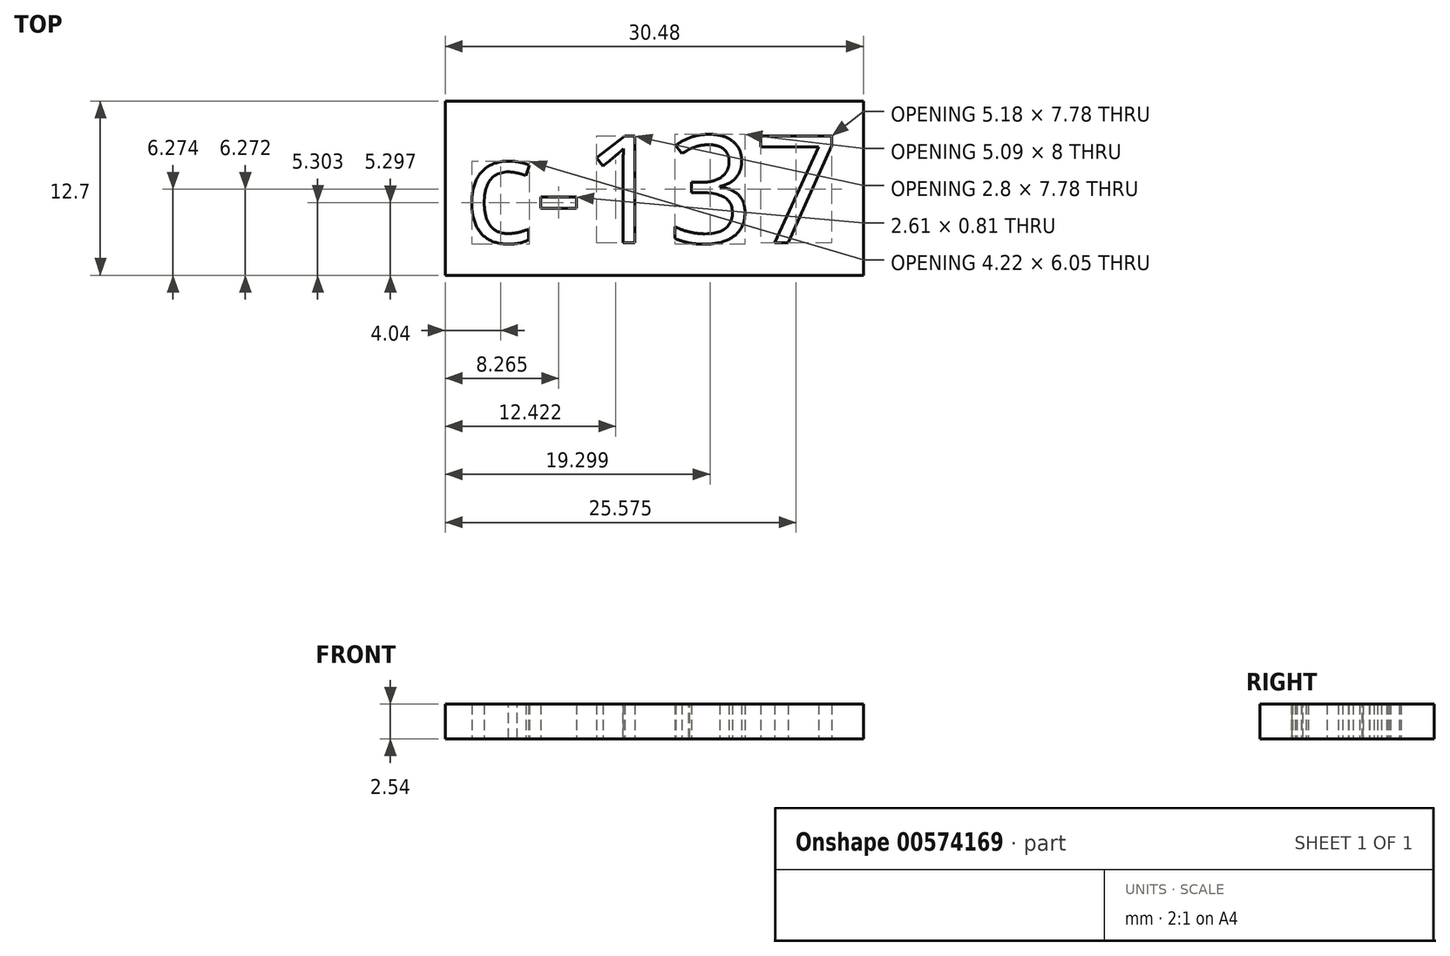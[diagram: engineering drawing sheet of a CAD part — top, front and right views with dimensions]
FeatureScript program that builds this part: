
annotation { "Feature Type Name" : "Feature", "Feature Type Description" : "" }
export const myFeature = defineFeature(function(context is Context, id is Id, definition is map)
    precondition{}
    {
        {
            var Q0;
            Q0=qCreatedBy(makeId("Top.planeOp"),FACE);
            var sketch = newSketch(context, id + "F0", { "sketchPlane" : qUnion([Q0])});
            skLineSegment(sketch, "E0.bottom", {"start": v(-16.62, 0) * mm, "end": v(13.86, 0) * mm});
            skLineSegment(sketch, "E0.top", {"start": v(-16.62, 12.7) * mm, "end": v(13.86, 12.7) * mm});
            skLineSegment(sketch, "E0.left", {"start": v(-16.62, 0) * mm, "end": v(-16.62, 12.7) * mm});
            skLineSegment(sketch, "E0.right", {"start": v(13.86, 0) * mm, "end": v(13.86, 12.7) * mm});
            skText(sketch, "E1", { "text": "c-137", "fontName": "OpenSans-Regular.ttf"});
            const initialGuessF0  = {"E1": [-0.0153, 0.00238, 1, 0, 0.00785]};
            skSetInitialGuess(sketch, initialGuessF0);
            skSolve(sketch);
        }
        {
            var Q0;
            Q0=makeQuery(id+"F0.imprint","IMPRINT",FACE,{"disambiguationData":[TD([[makeQuery(id+"F0.imprint","IMPRINT",EDGE,{"derivedFrom":sQuery(id+"F0.wireOp",EDGE,"E0.bottom")}),1.0]])]});
            extrude(context, id + "F1", {"entities" : qUnion([Q0]), "depth" : 2.54 * mm, "offsetDistance" : 25.4 * mm});
        }
    });
